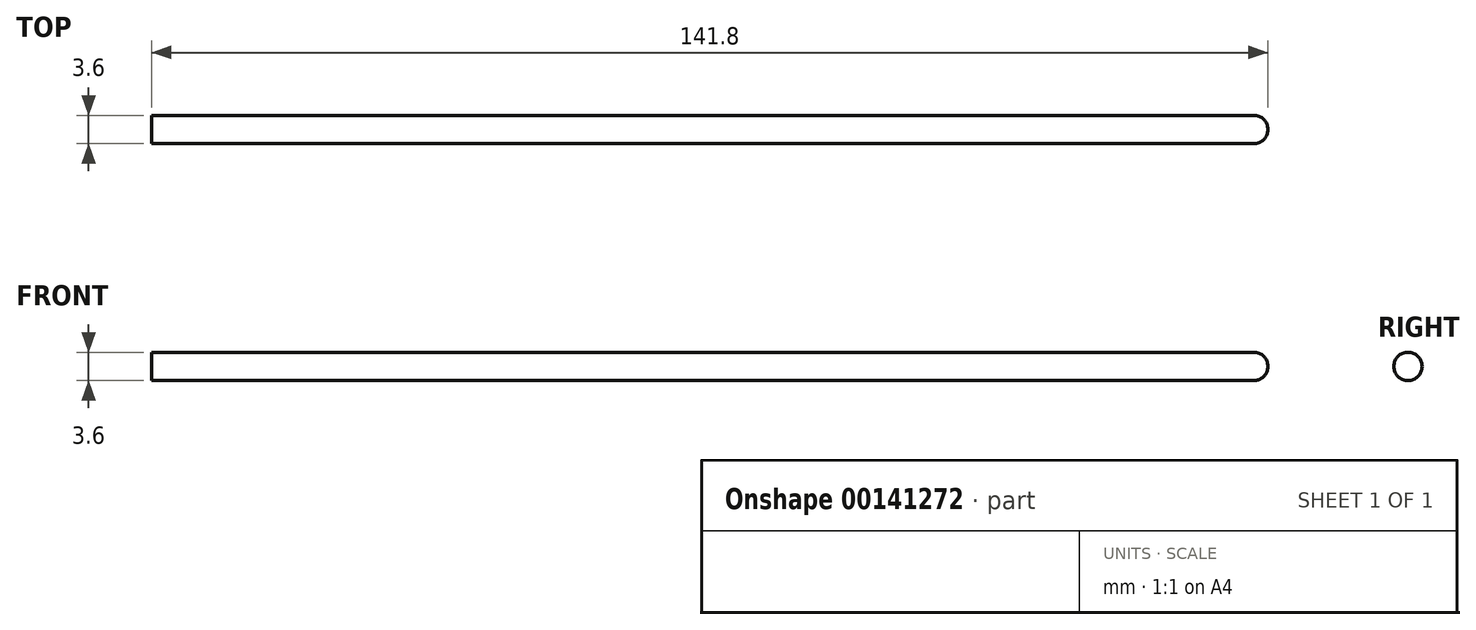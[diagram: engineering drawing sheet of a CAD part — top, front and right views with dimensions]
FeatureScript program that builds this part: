
annotation { "Feature Type Name" : "Feature", "Feature Type Description" : "" }
export const myFeature = defineFeature(function(context is Context, id is Id, definition is map)
    precondition{}
    {
        {
            var Q0;
            Q0=qCreatedBy(makeId("Front.planeOp"),FACE);
            var sketch = newSketch(context, id + "F0", { "sketchPlane" : qUnion([Q0])});
            skLineSegment(sketch, "E0", {"start": v(-13.1, 0) * mm, "end": v(-13.1, 1.8) * mm});
            skLineSegment(sketch, "E1", {"start": v(-13.1, 1.8) * mm, "end": v(126.9, 1.8) * mm});
            skLineSegment(sketch, "E2", {"start": v(126.9, 1.8) * mm, "end": v(126.9, 0) * mm});
            skLineSegment(sketch, "E3", {"start": v(126.9, 0) * mm, "end": v(-13.1, 0) * mm});
            skArc(sketch, "E4", {"start": v(128.7, 0) * mm, "mid": v(128.17, 1.27) * mm, "end": v(126.9, 1.8) * mm});
            skLineSegment(sketch, "E5", {"start": v(128.7, 0) * mm, "end": v(126.9, 0) * mm});
            skSolve(sketch);
        }
        {
            var Q0;
            Q0=makeQuery(id+"F0.imprint","IMPRINT",FACE,{"disambiguationData":[TD([[makeQuery(id+"F0.imprint","IMPRINT",EDGE,{"derivedFrom":sQuery(id+"F0.wireOp",EDGE,"E0")}),-1.0]])]});
            var Q1;
            Q1=makeQuery(id+"F0.imprint","IMPRINT",FACE,{"disambiguationData":[TD([[makeQuery(id+"F0.imprint","IMPRINT",EDGE,{"derivedFrom":sQuery(id+"F0.wireOp",EDGE,"E2")}),1.0]])]});
            var Q2;
            Q2=sQuery(id+"F0.wireOp",EDGE,"E3");
            revolve(context, id + "F1", {"entities" : qUnion([Q0, Q1]), "axis" : qUnion([Q2]), "revolveType" : RevolveType.FULL});
        }
    });
